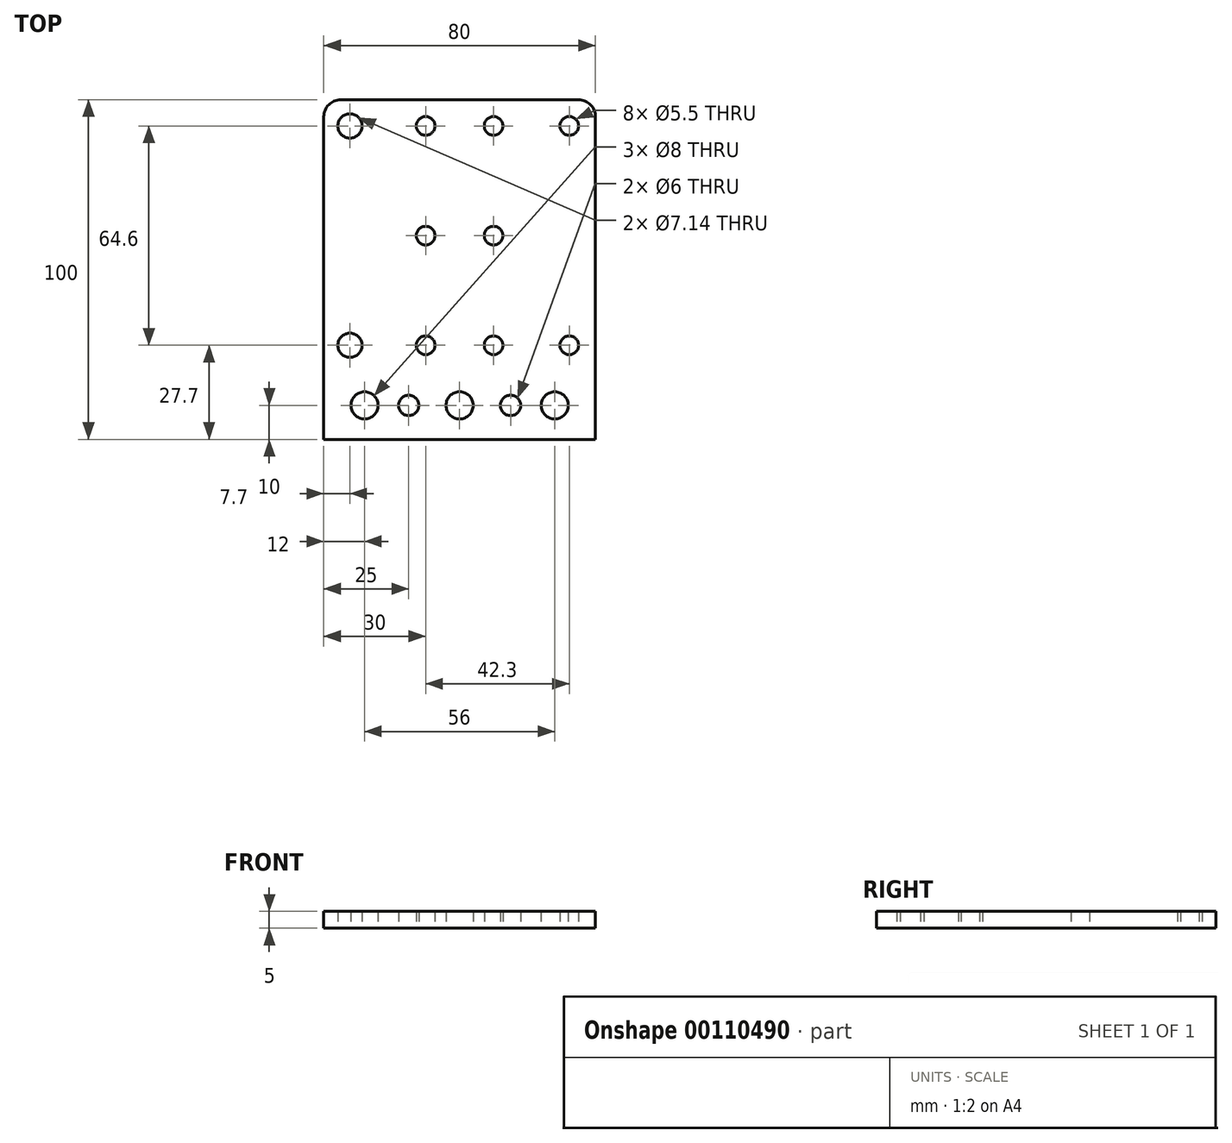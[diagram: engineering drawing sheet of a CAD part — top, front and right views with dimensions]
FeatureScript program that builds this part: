
annotation { "Feature Type Name" : "Feature", "Feature Type Description" : "" }
export const myFeature = defineFeature(function(context is Context, id is Id, definition is map)
    precondition{}
    {
        {
            var Q0;
            Q0=qCreatedBy(makeId("Top.planeOp"),FACE);
            var sketch = newSketch(context, id + "F0", { "sketchPlane" : qUnion([Q0])});
            skLineSegment(sketch, "E0.bottom", {"start": v(5, 0) * mm, "end": v(75, 0) * mm});
            skLineSegment(sketch, "E0.top", {"start": v(0, -100) * mm, "end": v(80, -100) * mm});
            skLineSegment(sketch, "E0.left", {"start": v(0, -5) * mm, "end": v(0, -100) * mm});
            skLineSegment(sketch, "E0.right", {"start": v(80, -5) * mm, "end": v(80, -100) * mm});
            skCircle(sketch, "E1", {"center": v(7.7, -7.7) * mm, "radius": 3.57 * mm});
            skCircle(sketch, "E2", {"center": v(72.3, -7.7) * mm, "radius": 2.75 * mm});
            skLineSegment(sketch, "E3", {"start": v(7.7, -7.7) * mm, "end": v(72.3, -7.7) * mm, "construction": true});
            skPoint(sketch, "E4.endSnap0", {"position": v(40, -7.7) * mm});
            skLineSegment(sketch, "E5", {"start": v(40, -7.7) * mm, "end": v(40, 0) * mm});
            skCircle(sketch, "E6", {"center": v(7.7, -72.3) * mm, "radius": 3.57 * mm});
            skCircle(sketch, "E7", {"center": v(72.3, -72.3) * mm, "radius": 2.75 * mm});
            skLineSegment(sketch, "E8", {"start": v(7.7, -72.3) * mm, "end": v(72.3, -72.3) * mm, "construction": true});
            skLineSegment(sketch, "E9", {"start": v(7.7, -7.7) * mm, "end": v(7.7, -72.3) * mm, "construction": true});
            skLineSegment(sketch, "E10", {"start": v(72.3, -7.7) * mm, "end": v(72.3, -72.3) * mm, "construction": true});
            skLineSegment(sketch, "E11", {"start": v(0, -80) * mm, "end": v(80, -80) * mm, "construction": true});
            skLineSegment(sketch, "E12", {"start": v(0, -90) * mm, "end": v(80, -90) * mm, "construction": true});
            skCircle(sketch, "E13", {"center": v(40, -90) * mm, "radius": 4 * mm});
            skCircle(sketch, "E14", {"center": v(68, -90) * mm, "radius": 4 * mm});
            skCircle(sketch, "E15", {"center": v(12, -90) * mm, "radius": 4 * mm});
            skLineSegment(sketch, "E16", {"start": v(40, -90) * mm, "end": v(40, -100) * mm, "construction": true});
            skCircle(sketch, "E17", {"center": v(25, -90) * mm, "radius": 3 * mm});
            skCircle(sketch, "E18", {"center": v(55, -90) * mm, "radius": 3 * mm});
            skLineSegment(sketch, "E19", {"start": v(40, -7.7) * mm, "end": v(40, -72.3) * mm, "construction": true});
            skLineSegment(sketch, "E20", {"start": v(7.7, -40) * mm, "end": v(72.3, -40) * mm, "construction": true});
            skCircle(sketch, "E21", {"center": v(30, -40) * mm, "radius": 2.75 * mm});
            skCircle(sketch, "E22", {"center": v(50, -40) * mm, "radius": 2.75 * mm});
            skCircle(sketch, "E23", {"center": v(30, -72.3) * mm, "radius": 2.75 * mm});
            skCircle(sketch, "E24", {"center": v(50, -72.3) * mm, "radius": 2.75 * mm});
            skLineSegment(sketch, "E25", {"start": v(30, -40) * mm, "end": v(30, -72.3) * mm, "construction": true});
            skLineSegment(sketch, "E26", {"start": v(50, -40) * mm, "end": v(50, -72.3) * mm, "construction": true});
            skLineSegment(sketch, "E27", {"start": v(30, -40) * mm, "end": v(30, -7.7) * mm, "construction": true});
            skLineSegment(sketch, "E28", {"start": v(50, -40) * mm, "end": v(50, -7.7) * mm, "construction": true});
            skCircle(sketch, "E29", {"center": v(30, -7.7) * mm, "radius": 2.75 * mm});
            skCircle(sketch, "E30", {"center": v(50, -7.7) * mm, "radius": 2.75 * mm});
            skPoint(sketch, "E31.visualSharp", {"position": v(0, 0) * mm});
            skArc(sketch, "E31.filletArc", {"start": v(5, 0) * mm, "mid": v(1.46, -1.46) * mm, "end": v(0, -5) * mm});
            skPoint(sketch, "E32.visualSharp", {"position": v(80, 0) * mm});
            skArc(sketch, "E32.filletArc", {"start": v(80, -5) * mm, "mid": v(78.54, -1.46) * mm, "end": v(75, 0) * mm});
            skSolve(sketch);
        }
        {
            var Q0;
            Q0 = qSketchRegion(id + "F0", true);
            extrude(context, id + "F1", {"entities" : qUnion([Q0]), "depth" : 5 * mm});
        }
    });
